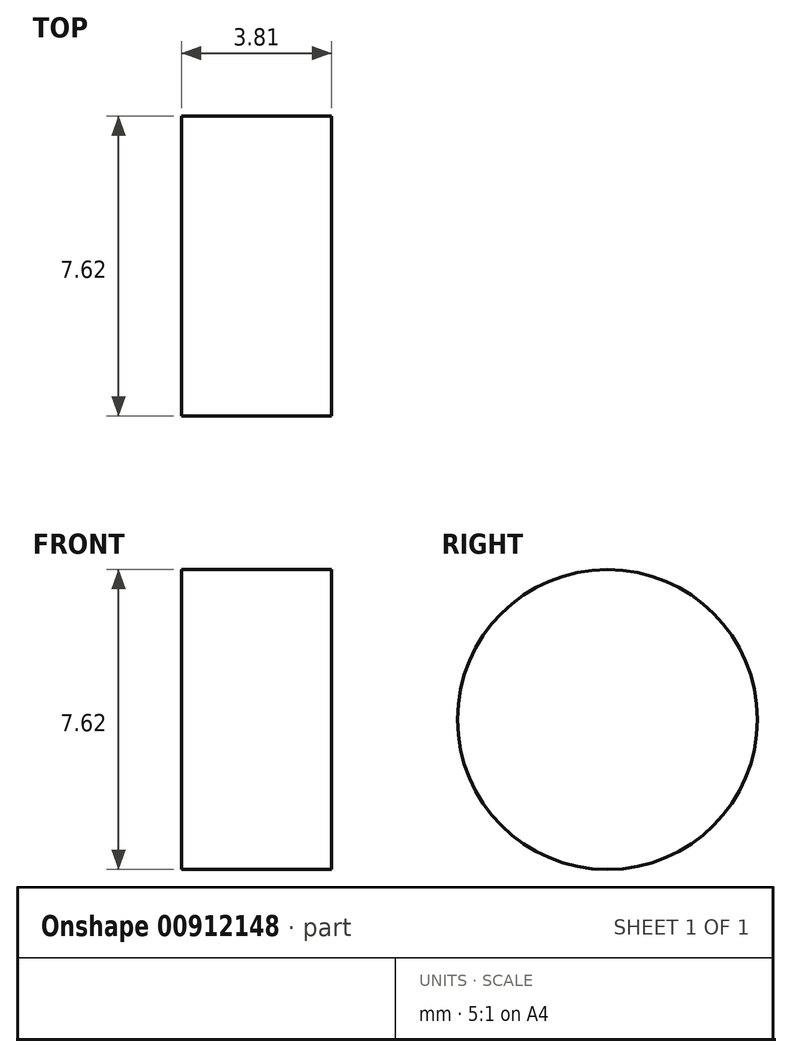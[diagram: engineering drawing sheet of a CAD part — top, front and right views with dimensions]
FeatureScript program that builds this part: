
annotation { "Feature Type Name" : "Feature", "Feature Type Description" : "" }
export const myFeature = defineFeature(function(context is Context, id is Id, definition is map)
    precondition{}
    {
        {
            var Q0;
            Q0=qCreatedBy(makeId("Right.planeOp"),FACE);
            var sketch = newSketch(context, id + "F0", { "sketchPlane" : qUnion([Q0])});
            skCircle(sketch, "E0", {"center": v(0, 0) * mm, "radius": 3.81 * mm});
            skSolve(sketch);
        }
        {
            var Q0;
            Q0 = qSketchRegion(id + "F0", true);
            extrude(context, id + "F1", {"entities" : qUnion([Q0]), "depth" : 3.8 * mm, "offsetDistance" : 25.4 * mm});
        }
    });
